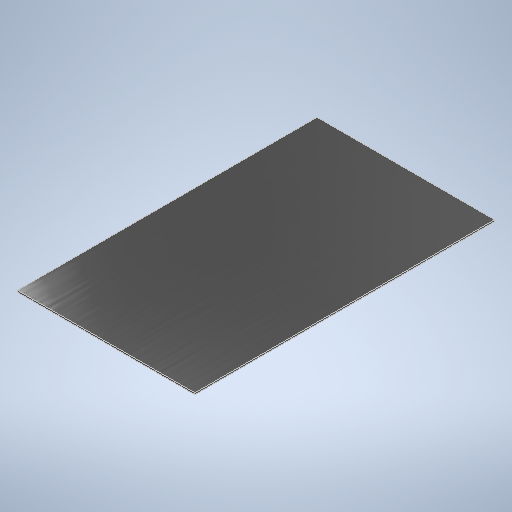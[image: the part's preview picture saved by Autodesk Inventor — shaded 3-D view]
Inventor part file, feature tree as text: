
AUTODESK INVENTOR PART (.ipt)
format: ipt  version: 2025.1 (Build 291241020, 241B)  size: 237,568 bytes
history: native  units: in
note: dims shown in document units (in); Inventor stores cm internally (conversion verified against a paired STEP export)
features: extrude x1, sketch x1
ambient origin geometry x8: Origin, YZ Plane, XZ Plane, XY Plane, X Axis, Y Axis, Z Axis, Center Point
bodies: Solid1 (feature_tree)
feature tree (2):
  extrude  "Extrusion1"  Depth=22.375in
  sketch  "Sketch1"  dims[d0=13.25in d1=22.375in d2=0.125in d3=0.0in]
